# Revit family: Table-Teknion-MXTGO-Gemstone_Base_Expansion_Meeting-R2023
name_source: partatom
category: Furniture
units: mm (PartAtom-declared; Revit-internal decimal feet)

## family parameters
Always vertical = Yes
Cut with Voids When Loaded = No
Enable Cutting in Views = No
OmniClass Number = 23.40.20.00
OmniClass Title = General Furniture and Specialties
Render Appearance Source = Family Geometry
Room Calculation Point = No
Shared = Yes
Work Plane-Based = No

## types (2) — shared parameters
Assembly Code = E2020200
Default Elevation = 0.000"
Manufacturer = Teknion
Manufacturer Fax = 416.661.4586
Part Number = MXTGO
Product Line = Expansion Meeting
Series = Meeting tables
Sustainability Data = https://www.teknion.com
URL = www.teknion.com
Unit Weight URL = http://www.teknion.com
Warranty = http://www.teknion.com

## per-type parameters (varying)
| type | Deep Knife Edge | Description | Flat Edge | Model |
| Flat Edge - Worksurface | No | Flat Edge, Meeting Table | Yes | MXTGOM______ |
| Deep Knife Edge - Worksurface | Yes | Deep Knife Edge, Meeting Table | No | MXTGOW______ |

## geometry (parser evidence)
native form markers: Sweep x2
no freeform markers — native parametric forms only
